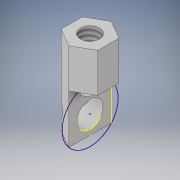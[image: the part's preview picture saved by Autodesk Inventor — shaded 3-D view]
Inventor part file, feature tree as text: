
AUTODESK INVENTOR PART (.ipt)
format: ipt  version: 2018 (Build 220112000, 112)  size: 143,872 bytes
history: native  units: in
note: dims shown in document units (in); Inventor stores cm internally (conversion verified against a paired STEP export)
features: sketch x5, extrude x2, hole x2
ambient origin geometry x8: Origin, YZ Plane, XZ Plane, XY Plane, X Axis, Y Axis, Z Axis, Center Point
bodies: Solid1 (feature_tree)
feature tree (9):
  extrude  "Extrusion1"  TaperAngle=90.0deg  [1 undecoded]
  hole  "Hole1"  [1 undecoded]
  extrude  "Extrusion2"  Depth=0.5in TaperAngle=0.0deg
  hole  "Hole2"  [1 undecoded]
  sketch  "Sketch7"  dims[d19=0.266in d20=0.5in d21=0.507in d22=0.25in d23=0.5635in d24=1.0in d25=0.8108in]
  sketch  "Sketch1"  dims[d0=0.1875in d1=90.0deg]
  sketch  "Sketch2"  dims[d2=2.3622in d4=360.0deg d6=0.9in d7=0.0in]
  sketch  "Sketch3"  dims[d8=0.196in d9=0.25in d10=0.375in d11=0.25in d12=0.5635in d13=0.5in d14=0.8108in d15=0.5in d16=0.0in]
  sketch  "Sketch5"  dims[d17=0.1875in d18=0.266in]
note: 3 required parameter values undecoded (feature->parameter linkage not recoverable at this tier; creation-order binding heuristic only, values carry confidence <= 0.55)
